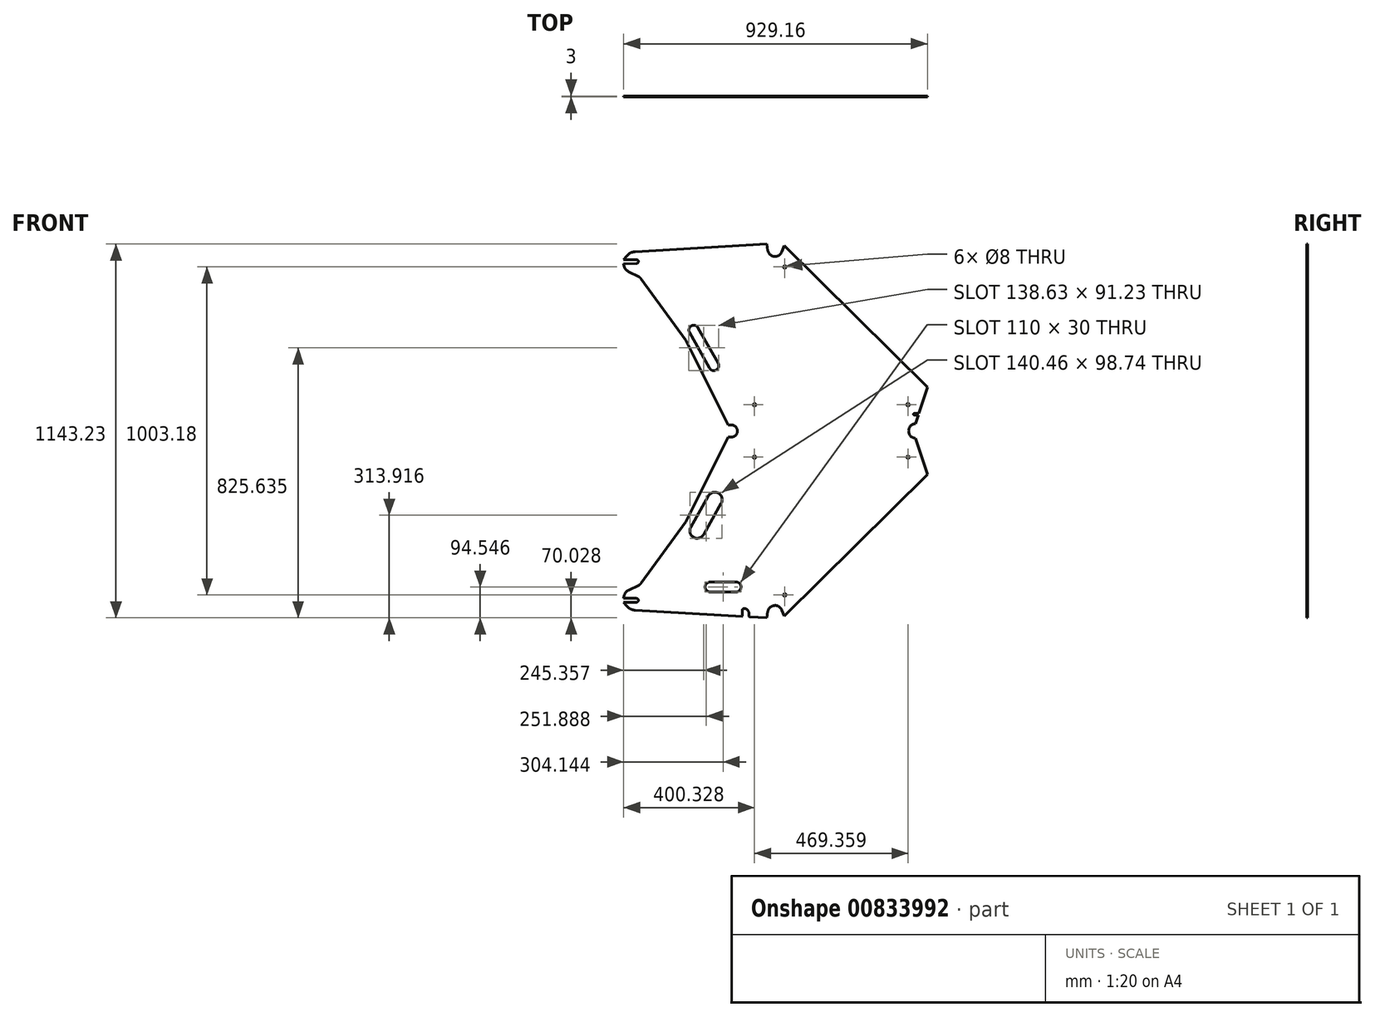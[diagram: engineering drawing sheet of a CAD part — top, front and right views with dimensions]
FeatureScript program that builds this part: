
annotation { "Feature Type Name" : "Feature", "Feature Type Description" : "" }
export const myFeature = defineFeature(function(context is Context, id is Id, definition is map)
    precondition{}
    {
        {
            var Q0;
            Q0=qCreatedBy(makeId("Front.planeOp"),FACE);
            var sketch = newSketch(context, id + "F0", { "sketchPlane" : qUnion([Q0])});
            skLineSegment(sketch, "E0", {"start": v(-160.76, 555.88) * mm, "end": v(408.24, 555.88) * mm, "construction": true});
            skLineSegment(sketch, "E1", {"start": v(408.24, 555.88) * mm, "end": v(445.83, 440.87) * mm, "construction": true});
            skArc(sketch, "E2", {"start": v(0.74, 26.27) * mm, "mid": v(-22.4, 40.64) * mm, "end": v(-42.43, 22.2) * mm});
            skLineSegment(sketch, "E3", {"start": v(-20.28, 18.24) * mm, "end": v(-144.86, 555.88) * mm, "construction": true});
            skLineSegment(sketch, "E4", {"start": v(-160.76, 555.88) * mm, "end": v(-39.05, 30.64) * mm, "construction": true});
            skLineSegment(sketch, "E5", {"start": v(-128.12, 555.88) * mm, "end": v(-7.89, 37.02) * mm, "construction": true});
            skLineSegment(sketch, "E6", {"start": v(0, 0) * mm, "end": v(-484.19, 28.1) * mm, "construction": true});
            skLineSegment(sketch, "E7", {"start": v(-160.76, 555.88) * mm, "end": v(-484.19, 28.1) * mm, "construction": true});
            skLineSegment(sketch, "E8", {"start": v(445.83, 440.87) * mm, "end": v(0, 0) * mm, "construction": true});
            skPoint(sketch, "E9", {"position": v(-176.43, 530.3) * mm});
            skPoint(sketch, "E10", {"position": v(-312.28, 308.61) * mm});
            skLineSegment(sketch, "E11", {"start": v(-312.28, 308.61) * mm, "end": v(-292.67, 296.6) * mm, "construction": true});
            skLineSegment(sketch, "E12", {"start": v(-176.43, 530.3) * mm, "end": v(-292.67, 296.6) * mm});
            skLineSegment(sketch, "E13", {"start": v(-429.8, 108.64) * mm, "end": v(-292.67, 296.6) * mm});
            skLineSegment(sketch, "E14", {"start": v(397.8, 555.88) * mm, "end": v(-163.71, 555.88) * mm});
            skLineSegment(sketch, "E15", {"start": v(409.57, 551.8) * mm, "end": v(445.83, 440.87) * mm});
            skLineSegment(sketch, "E16", {"start": v(445.83, 440.87) * mm, "end": v(7.82, 7.73) * mm});
            skPoint(sketch, "E17", {"position": v(-45.92, 2.66) * mm});
            skPoint(sketch, "E18", {"position": v(7.82, 7.73) * mm});
            skArc(sketch, "E19", {"start": v(7.82, 7.73) * mm, "mid": v(-23.1, 48.1) * mm, "end": v(-45.92, 2.66) * mm, "construction": true});
            skLineSegment(sketch, "E20", {"start": v(-176.43, 530.3) * mm, "end": v(-163.71, 555.88) * mm});
            skLineSegment(sketch, "E21", {"start": v(-173.75, 373) * mm, "end": v(-249.95, 238.03) * mm, "construction": true});
            skLineSegment(sketch, "E22", {"start": v(-186.81, 380.38) * mm, "end": v(-263, 245.4) * mm, "construction": true});
            skPoint(sketch, "E23.visualSharp", {"position": v(-289.13, 260.15) * mm});
            skPoint(sketch, "E24.visualSharp", {"position": v(-249.95, 238.03) * mm});
            skLineSegment(sketch, "E25", {"start": v(-212.94, 395.13) * mm, "end": v(-289.13, 260.15) * mm, "construction": true});
            skLineSegment(sketch, "E26", {"start": v(-249.95, 238.03) * mm, "end": v(-289.13, 260.15) * mm, "construction": true});
            skLineSegment(sketch, "E27", {"start": v(-212.94, 395.13) * mm, "end": v(-173.75, 373) * mm, "construction": true});
            skLineSegment(sketch, "E28", {"start": v(-292.67, 296.6) * mm, "end": v(-274.39, 286.27) * mm, "construction": true});
            skArc(sketch, "E29", {"start": v(-278.07, 279.74) * mm, "mid": v(-269.54, 249.09) * mm, "end": v(-238.88, 257.62) * mm});
            skLineSegment(sketch, "E30", {"start": v(-278.07, 279.74) * mm, "end": v(-238.88, 257.62) * mm, "construction": true});
            skArc(sketch, "E31", {"start": v(-184.81, 353.41) * mm, "mid": v(-193.34, 384.07) * mm, "end": v(-224, 375.53) * mm});
            skLineSegment(sketch, "E32", {"start": v(-224, 375.53) * mm, "end": v(-184.81, 353.41) * mm, "construction": true});
            skLineSegment(sketch, "E33", {"start": v(-278.07, 279.74) * mm, "end": v(-224, 375.53) * mm});
            skLineSegment(sketch, "E34", {"start": v(-184.81, 353.41) * mm, "end": v(-238.88, 257.62) * mm});
            skLineSegment(sketch, "E35.bottom", {"start": v(-234.19, 112.2) * mm, "end": v(-124.19, 112.2) * mm, "construction": true});
            skLineSegment(sketch, "E35.top", {"start": v(-234.19, 82.2) * mm, "end": v(-124.19, 82.2) * mm, "construction": true});
            skLineSegment(sketch, "E35.left", {"start": v(-234.19, 112.2) * mm, "end": v(-234.19, 82.2) * mm, "construction": true});
            skLineSegment(sketch, "E35.right", {"start": v(-124.19, 112.2) * mm, "end": v(-124.19, 82.2) * mm, "construction": true});
            skLineSegment(sketch, "E36", {"start": v(-124.19, 82.2) * mm, "end": v(-124.19, 7.2) * mm, "construction": true});
            skArc(sketch, "E37", {"start": v(-219.19, 112.2) * mm, "mid": v(-234.19, 97.2) * mm, "end": v(-219.19, 82.2) * mm});
            skArc(sketch, "E38", {"start": v(-139.19, 82.2) * mm, "mid": v(-124.19, 97.2) * mm, "end": v(-139.19, 112.2) * mm});
            skLineSegment(sketch, "E39", {"start": v(-139.19, 112.2) * mm, "end": v(-139.19, 82.2) * mm, "construction": true});
            skLineSegment(sketch, "E40", {"start": v(-219.19, 112.2) * mm, "end": v(-139.19, 112.2) * mm});
            skLineSegment(sketch, "E41", {"start": v(-139.19, 82.2) * mm, "end": v(-219.19, 82.2) * mm});
            skLineSegment(sketch, "E42", {"start": v(-641.86, 574.28) * mm, "end": v(862.04, 574.28) * mm, "construction": true});
            skLineSegment(sketch, "E43.MirrorCS", {"start": v(-312.28, 839.94) * mm, "end": v(-292.67, 851.96) * mm, "construction": true});
            skLineSegment(sketch, "E44.MirrorCS", {"start": v(-176.43, 618.26) * mm, "end": v(-163.71, 592.68) * mm});
            skLineSegment(sketch, "E45.MirrorCS", {"start": v(-249.95, 910.53) * mm, "end": v(-289.13, 888.41) * mm, "construction": true});
            skLineSegment(sketch, "E46.MirrorCS", {"start": v(-447.54, 1122.59) * mm, "end": v(-461.2, 1082.95) * mm, "construction": true});
            skLineSegment(sketch, "E47.MirrorCS", {"start": v(-212.94, 753.43) * mm, "end": v(-173.75, 775.55) * mm, "construction": true});
            skLineSegment(sketch, "E48.MirrorCS", {"start": v(-292.67, 851.96) * mm, "end": v(-274.39, 862.29) * mm, "construction": true});
            skLineSegment(sketch, "E49.MirrorCS", {"start": v(-45.92, 1145.9) * mm, "end": v(-447.54, 1122.59) * mm});
            skArc(sketch, "E50.MirrorC", {"start": v(0.74, 1122.29) * mm, "mid": v(-22.4, 1107.92) * mm, "end": v(-42.43, 1126.36) * mm});
            skLineSegment(sketch, "E51.MirrorCS", {"start": v(445.83, 707.7) * mm, "end": v(7.82, 1140.82) * mm});
            skLineSegment(sketch, "E52.MirrorCS", {"start": v(397.8, 592.68) * mm, "end": v(-163.71, 592.68) * mm});
            skLineSegment(sketch, "E53.MirrorCS", {"start": v(409.57, 596.75) * mm, "end": v(418.05, 622.68) * mm});
            skArc(sketch, "E54.MirrorCS", {"start": v(7.82, 1140.82) * mm, "mid": v(-23.1, 1100.45) * mm, "end": v(-45.92, 1145.9) * mm, "construction": true});
            skPoint(sketch, "E55.MirrorP", {"position": v(-289.13, 888.41) * mm});
            skLineSegment(sketch, "E56.MirrorCS", {"start": v(-20.28, 1130.32) * mm, "end": v(-144.86, 592.68) * mm, "construction": true});
            skPoint(sketch, "E57.MirrorP", {"position": v(-312.28, 839.94) * mm});
            skLineSegment(sketch, "E58.MirrorCS", {"start": v(-128.12, 592.68) * mm, "end": v(-7.89, 1111.54) * mm, "construction": true});
            skPoint(sketch, "E59.MirrorP", {"position": v(-176.43, 618.26) * mm});
            skPoint(sketch, "E60.MirrorP", {"position": v(-45.92, 1145.9) * mm});
            skLineSegment(sketch, "E61.MirrorCS", {"start": v(-160.76, 592.68) * mm, "end": v(397.8, 592.68) * mm, "construction": true});
            skPoint(sketch, "E62.MirrorP", {"position": v(7.82, 1140.82) * mm});
            skLineSegment(sketch, "E63.MirrorCS", {"start": v(-160.76, 592.68) * mm, "end": v(-39.05, 1117.92) * mm, "construction": true});
            skLineSegment(sketch, "E64.MirrorCS", {"start": v(-160.76, 592.68) * mm, "end": v(-484.19, 1120.46) * mm, "construction": true});
            skLineSegment(sketch, "E65.MirrorCS", {"start": v(-186.81, 768.18) * mm, "end": v(-263, 903.16) * mm, "construction": true});
            skPoint(sketch, "E66.MirrorP", {"position": v(-249.95, 910.53) * mm});
            skPoint(sketch, "E67.MirrorP", {"position": v(-461.2, 1082.95) * mm});
            skLineSegment(sketch, "E68.MirrorCS", {"start": v(445.83, 707.7) * mm, "end": v(0, 1148.56) * mm, "construction": true});
            skLineSegment(sketch, "E69.MirrorCS", {"start": v(409.57, 596.75) * mm, "end": v(418.05, 622.68) * mm, "construction": true});
            skLineSegment(sketch, "E70.MirrorCS", {"start": v(-461.2, 1082.95) * mm, "end": v(-292.67, 851.96) * mm});
            skLineSegment(sketch, "E71.MirrorCS", {"start": v(-176.43, 618.26) * mm, "end": v(-178.63, 622.68) * mm});
            skLineSegment(sketch, "E72.MirrorCS", {"start": v(0, 1148.56) * mm, "end": v(-484.19, 1120.46) * mm, "construction": true});
            skLineSegment(sketch, "E73", {"start": v(-255.63, 890.1) * mm, "end": v(-194.19, 781.24) * mm});
            skArc(sketch, "E74", {"start": v(-255.63, 890.1) * mm, "mid": v(-276.07, 895.78) * mm, "end": v(-281.76, 875.35) * mm});
            skLineSegment(sketch, "E75", {"start": v(-289.13, 888.41) * mm, "end": v(-212.94, 753.43) * mm, "construction": true});
            skLineSegment(sketch, "E76", {"start": v(-281.76, 875.35) * mm, "end": v(-255.63, 890.1) * mm, "construction": true});
            skArc(sketch, "E77", {"start": v(-220.31, 766.5) * mm, "mid": v(-199.88, 760.8) * mm, "end": v(-194.19, 781.24) * mm});
            skLineSegment(sketch, "E78", {"start": v(-220.31, 766.5) * mm, "end": v(-194.19, 781.24) * mm, "construction": true});
            skLineSegment(sketch, "E79", {"start": v(-281.76, 875.35) * mm, "end": v(-220.31, 766.5) * mm});
            skArc(sketch, "E80.trimOffspring", {"start": v(-153.71, 555.88) * mm, "mid": v(-135.31, 574.28) * mm, "end": v(-153.71, 592.68) * mm});
            skArc(sketch, "E81", {"start": v(409.57, 596.75) * mm, "mid": v(388.24, 574.28) * mm, "end": v(409.57, 551.8) * mm});
            skLineSegment(sketch, "E82", {"start": v(388.24, 592.68) * mm, "end": v(388.24, 555.88) * mm, "construction": true});
            skPoint(sketch, "E83.orphan", {"position": v(408.24, 592.68) * mm});
            skPoint(sketch, "E84.orphan", {"position": v(408.24, 555.88) * mm});
            skLineSegment(sketch, "E85", {"start": v(-437.04, 102.52) * mm, "end": v(-516.22, 63.05) * mm, "construction": true});
            skLineSegment(sketch, "E86", {"start": v(-516.22, 63.05) * mm, "end": v(-444.22, 62.36) * mm, "construction": true});
            skLineSegment(sketch, "E87", {"start": v(-438.28, 56.3) * mm, "end": v(-438.28, 56.3) * mm});
            skLineSegment(sketch, "E88", {"start": v(-444.33, 50.36) * mm, "end": v(-483.33, 50.74) * mm});
            skLineSegment(sketch, "E89", {"start": v(-483.33, 50.74) * mm, "end": v(-463.52, 26.9) * mm});
            skPoint(sketch, "E90.orphan", {"position": v(-439.25, 101.42) * mm});
            skPoint(sketch, "E91.end.orphan", {"position": v(-461.2, 65.61) * mm});
            skArc(sketch, "E92", {"start": v(-467.98, 87.1) * mm, "mid": v(-479.03, 77.06) * mm, "end": v(-483.22, 62.74) * mm});
            skLineSegment(sketch, "E93", {"start": v(-483.22, 62.74) * mm, "end": v(-482.71, 115.9) * mm, "construction": true});
            skPoint(sketch, "E94.visualSharp", {"position": v(-438.22, 62.3) * mm});
            skArc(sketch, "E94.filletArc", {"start": v(-438.28, 56.3) * mm, "mid": v(-440, 60.57) * mm, "end": v(-444.22, 62.36) * mm});
            skPoint(sketch, "E95.visualSharp", {"position": v(-438.33, 50.3) * mm});
            skArc(sketch, "E95.filletArc", {"start": v(-444.33, 50.36) * mm, "mid": v(-440.07, 52.08) * mm, "end": v(-438.28, 56.3) * mm});
            skLineSegment(sketch, "E96", {"start": v(-467.98, 87.1) * mm, "end": v(-437.04, 102.52) * mm, "construction": true});
            skLineSegment(sketch, "E97", {"start": v(-467.98, 87.1) * mm, "end": v(-437.04, 102.52) * mm});
            skLineSegment(sketch, "E98", {"start": v(-483.22, 62.74) * mm, "end": v(-444.22, 62.36) * mm});
            skLineSegment(sketch, "E99", {"start": v(-463.52, 26.9) * mm, "end": v(-447.54, 25.97) * mm, "construction": true});
            skArc(sketch, "E100", {"start": v(-473.74, 39.2) * mm, "mid": v(-462.02, 29.86) * mm, "end": v(-447.54, 25.97) * mm});
            skLineSegment(sketch, "E101", {"start": v(-483.22, 62.74) * mm, "end": v(-483.33, 50.74) * mm, "construction": true});
            skPoint(sketch, "E102.visualSharp", {"position": v(-432.68, 104.7) * mm});
            skArc(sketch, "E102.filletArc", {"start": v(-437.04, 102.52) * mm, "mid": v(-433.06, 105.15) * mm, "end": v(-429.8, 108.64) * mm});
            skLineSegment(sketch, "E103.MirrorCS", {"start": v(-467.98, 1061.46) * mm, "end": v(-437.04, 1046.03) * mm});
            skLineSegment(sketch, "E104.MirrorCS", {"start": v(-483.22, 1085.82) * mm, "end": v(-444.22, 1086.2) * mm});
            skArc(sketch, "E105.MirrorCS", {"start": v(-444.33, 1098.2) * mm, "mid": v(-440.07, 1096.48) * mm, "end": v(-438.28, 1092.25) * mm});
            skArc(sketch, "E106.MirrorCS", {"start": v(-438.28, 1092.25) * mm, "mid": v(-440, 1088) * mm, "end": v(-444.22, 1086.2) * mm});
            skArc(sketch, "E107.MirrorCS", {"start": v(-437.04, 1046.03) * mm, "mid": v(-433.06, 1043.41) * mm, "end": v(-429.8, 1039.92) * mm});
            skLineSegment(sketch, "E108.MirrorCS", {"start": v(-444.33, 1098.2) * mm, "end": v(-483.33, 1097.82) * mm});
            skLineSegment(sketch, "E109.MirrorCS", {"start": v(-463.52, 1121.66) * mm, "end": v(-447.54, 1122.59) * mm, "construction": true});
            skPoint(sketch, "E110.MirrorP", {"position": v(-438.22, 1086.25) * mm});
            skArc(sketch, "E111.MirrorCS", {"start": v(-473.74, 1109.36) * mm, "mid": v(-462.02, 1118.7) * mm, "end": v(-447.54, 1122.59) * mm});
            skLineSegment(sketch, "E112.MirrorCS", {"start": v(-516.22, 1085.5) * mm, "end": v(-444.22, 1086.2) * mm, "construction": true});
            skLineSegment(sketch, "E113.MirrorCS", {"start": v(-483.22, 1085.82) * mm, "end": v(-482.71, 1032.66) * mm, "construction": true});
            skArc(sketch, "E114.MirrorCS", {"start": v(-467.98, 1061.46) * mm, "mid": v(-479.03, 1071.5) * mm, "end": v(-483.22, 1085.82) * mm});
            skLineSegment(sketch, "E115.MirrorCS", {"start": v(-483.33, 1097.82) * mm, "end": v(-463.52, 1121.66) * mm});
            skPoint(sketch, "E116.MirrorP", {"position": v(-432.68, 1043.86) * mm});
            skPoint(sketch, "E117.MirrorP", {"position": v(-438.33, 1098.25) * mm});
            skLineSegment(sketch, "E118.MirrorCS", {"start": v(-467.98, 1061.46) * mm, "end": v(-437.04, 1046.03) * mm, "construction": true});
            skLineSegment(sketch, "E119.MirrorCS", {"start": v(-437.04, 1046.03) * mm, "end": v(-516.22, 1085.5) * mm, "construction": true});
            skLineSegment(sketch, "E120.MirrorCS", {"start": v(-483.22, 1085.82) * mm, "end": v(-483.33, 1097.82) * mm, "construction": true});
            skPoint(sketch, "E121.MirrorP", {"position": v(-439.25, 1047.14) * mm});
            skLineSegment(sketch, "E122", {"start": v(-99.29, 30.8) * mm, "end": v(-114.61, 31.7) * mm});
            skCircle(sketch, "E123", {"center": v(-20.28, 18.24) * mm, "radius": 100 * mm, "construction": true});
            skCircle(sketch, "E124", {"center": v(-20.28, 18.24) * mm, "radius": 80 * mm, "construction": true});
            skArc(sketch, "E125", {"start": v(-119.88, 27.15) * mm, "mid": v(-120.27, 17.04) * mm, "end": v(-119.64, 6.94) * mm});
            skArc(sketch, "E126", {"start": v(-99.29, 30.8) * mm, "mid": v(-100.28, 18.28) * mm, "end": v(-99.3, 5.76) * mm});
            skPoint(sketch, "E127.visualSharp", {"position": v(-119.33, 31.97) * mm});
            skArc(sketch, "E127.filletArc", {"start": v(-114.61, 31.7) * mm, "mid": v(-118.17, 30.49) * mm, "end": v(-119.88, 27.15) * mm});
            skLineSegment(sketch, "E128", {"start": v(-119.64, 6.94) * mm, "end": v(-447.54, 25.97) * mm});
            skLineSegment(sketch, "E129", {"start": v(-99.3, 5.76) * mm, "end": v(-45.92, 2.66) * mm});
            skCircle(sketch, "E130", {"center": v(-83, 654.48) * mm, "radius": 4 * mm});
            skCircle(sketch, "E131", {"center": v(386.36, 654.48) * mm, "radius": 4 * mm});
            skCircle(sketch, "E132", {"center": v(9.5, 1075.87) * mm, "radius": 4 * mm});
            skLineSegment(sketch, "E133", {"start": v(-120.75, 624.48) * mm, "end": v(418.63, 624.48) * mm, "construction": true});
            skLineSegment(sketch, "E134", {"start": v(437.88, 715.55) * mm, "end": v(397.7, 592.61) * mm, "construction": true});
            skLineSegment(sketch, "E135", {"start": v(0, 1108.22) * mm, "end": v(435.87, 677.2) * mm, "construction": true});
            skCircle(sketch, "E136.MirrorC", {"center": v(9.5, 72.69) * mm, "radius": 4 * mm});
            skCircle(sketch, "E137.MirrorC", {"center": v(-83, 494.08) * mm, "radius": 4 * mm});
            skCircle(sketch, "E138.MirrorC", {"center": v(386.36, 494.08) * mm, "radius": 4 * mm});
            skLineSegment(sketch, "E139", {"start": v(-153.71, 592.68) * mm, "end": v(-153.71, 555.88) * mm, "construction": true});
            skLineSegment(sketch, "E140", {"start": v(-42.43, 22.2) * mm, "end": v(-45.92, 2.66) * mm});
            skLineSegment(sketch, "E141", {"start": v(0.74, 26.27) * mm, "end": v(7.82, 7.73) * mm});
            skLineSegment(sketch, "E142", {"start": v(-45.92, 1145.9) * mm, "end": v(-42.43, 1126.36) * mm});
            skLineSegment(sketch, "E143", {"start": v(0.74, 1122.29) * mm, "end": v(7.82, 1140.82) * mm});
            skArc(sketch, "E144", {"start": v(-100.27, 16.77) * mm, "mid": v(-104.51, 27.04) * mm, "end": v(-114.61, 31.7) * mm});
            skLineSegment(sketch, "E145", {"start": v(-530.7, 62.82) * mm, "end": v(-438.1, 61.94) * mm, "construction": true});
            skLineSegment(sketch, "E146", {"start": v(-438.1, 61.94) * mm, "end": v(-438.2, 50.97) * mm, "construction": true});
            skLineSegment(sketch, "E147", {"start": v(-438.2, 50.97) * mm, "end": v(-529.63, 51.84) * mm, "construction": true});
            skLineSegment(sketch, "E148.trimOffspring", {"start": v(-178.63, 622.68) * mm, "end": v(-292.67, 851.96) * mm});
            skLineSegment(sketch, "E149", {"start": v(431.28, 622.68) * mm, "end": v(406.05, 622.68) * mm, "construction": true});
            skLineSegment(sketch, "E150", {"start": v(418.05, 622.68) * mm, "end": v(403.05, 622.68) * mm});
            skLineSegment(sketch, "E151", {"start": v(403.05, 625.68) * mm, "end": v(403.05, 625.68) * mm});
            skLineSegment(sketch, "E152", {"start": v(406.05, 628.68) * mm, "end": v(420, 628.68) * mm});
            skPoint(sketch, "E153.visualSharp", {"position": v(403.05, 628.68) * mm});
            skArc(sketch, "E153.filletArc", {"start": v(406.05, 628.68) * mm, "mid": v(403.92, 627.8) * mm, "end": v(403.05, 625.68) * mm});
            skPoint(sketch, "E154.newPointA", {"position": v(403.05, 622.68) * mm});
            skArc(sketch, "E154.filletArc", {"start": v(403.05, 625.68) * mm, "mid": v(403.92, 623.56) * mm, "end": v(406.05, 622.68) * mm});
            skLineSegment(sketch, "E155.trimOffspring", {"start": v(420, 628.68) * mm, "end": v(445.83, 707.7) * mm, "construction": true});
            skLineSegment(sketch, "E156.trimOffspring", {"start": v(420, 628.68) * mm, "end": v(445.83, 707.7) * mm});
            skSolve(sketch);
        }
        {
            var Q0;
            Q0=qSketchRegion(id+"F0",true);
            extrude(context, id + "F1", {"entities" : qUnion([Q0]), "depth" : 3 * mm, "offsetDistance" : 25 * mm});
        }
    });
